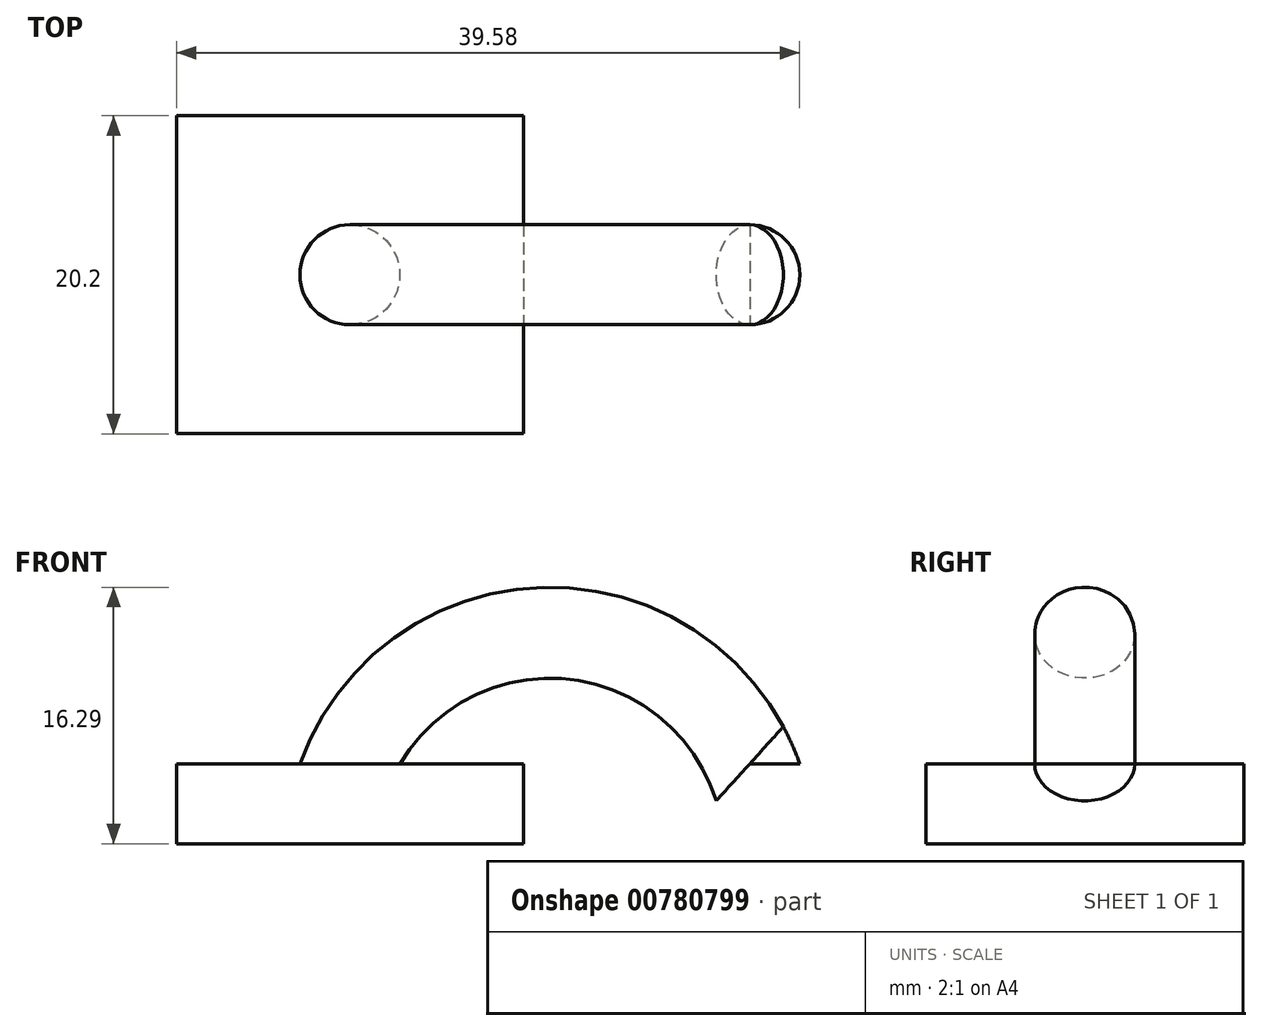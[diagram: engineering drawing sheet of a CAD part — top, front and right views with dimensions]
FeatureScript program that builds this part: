
annotation { "Feature Type Name" : "Feature", "Feature Type Description" : "" }
export const myFeature = defineFeature(function(context is Context, id is Id, definition is map)
    precondition{}
    {
        {
            var Q0;
            Q0=qCreatedBy(makeId("Top.planeOp"),FACE);
            var sketch = newSketch(context, id + "F0", { "sketchPlane" : qUnion([Q0])});
            skCircle(sketch, "E0", {"center": v(0, 0) * mm, "radius": 3.18 * mm});
            skCircle(sketch, "E1", {"center": v(25.4, 0) * mm, "radius": 3.18 * mm});
            skSolve(sketch);
        }
        {
            var Q0;
            Q0=qCreatedBy(makeId("Front.planeOp"),FACE);
            var sketch = newSketch(context, id + "F1", { "sketchPlane" : qUnion([Q0])});
            skArc(sketch, "E2", {"start": v(25.4, 0) * mm, "mid": v(12.7, 8.26) * mm, "end": v(0, 0) * mm});
            skSolve(sketch);
        }
        {
            var Q0;
            Q0=makeQuery(id+"F0.imprint","IMPRINT",FACE,{"disambiguationData":[TD([[makeQuery(id+"F0.imprint","IMPRINT",EDGE,{"derivedFrom":sQuery(id+"F0.wireOp",EDGE,"E0")}),1.0]])]});
            var Q1;
            Q1=makeQuery(id+"F0.imprint","IMPRINT",FACE,{"disambiguationData":[TD([[makeQuery(id+"F0.imprint","IMPRINT",EDGE,{"derivedFrom":sQuery(id+"F0.wireOp",EDGE,"E1")}),1.0]])]});
            var Q2;
            Q2=sQuery(id+"F1.wireOp",EDGE,"E2");
            sweep(context, id + "F2", {"profiles" : qUnion([Q0, Q1]), "path" : qUnion([Q2])});
        }
        {
            var Q0;
            Q0=qCreatedBy(makeId("Top.planeOp"),FACE);
            var sketch = newSketch(context, id + "F3", { "sketchPlane" : qUnion([Q0])});
            skLineSegment(sketch, "E3.bottom", {"start": v(11.01, 10.1) * mm, "end": v(-11.01, 10.1) * mm});
            skLineSegment(sketch, "E3.top", {"start": v(11.01, -10.1) * mm, "end": v(-11.01, -10.1) * mm});
            skLineSegment(sketch, "E3.left", {"start": v(11.01, 10.1) * mm, "end": v(11.01, -10.1) * mm});
            skLineSegment(sketch, "E3.right", {"start": v(-11.01, 10.1) * mm, "end": v(-11.01, -10.1) * mm});
            skPoint(sketch, "E3.middle", {"position": v(0, 0) * mm});
            skSolve(sketch);
        }
        {
            var Q0;
            Q0 = qSketchRegion(id + "F3", true);
            extrude(context, id + "F4", {"entities" : qUnion([Q0]), "operationType" : NewBodyOperationType.ADD, "oppositeDirection" : true, "depth" : 5.08 * mm, "offsetDistance" : 25.4 * mm});
        }
    });
